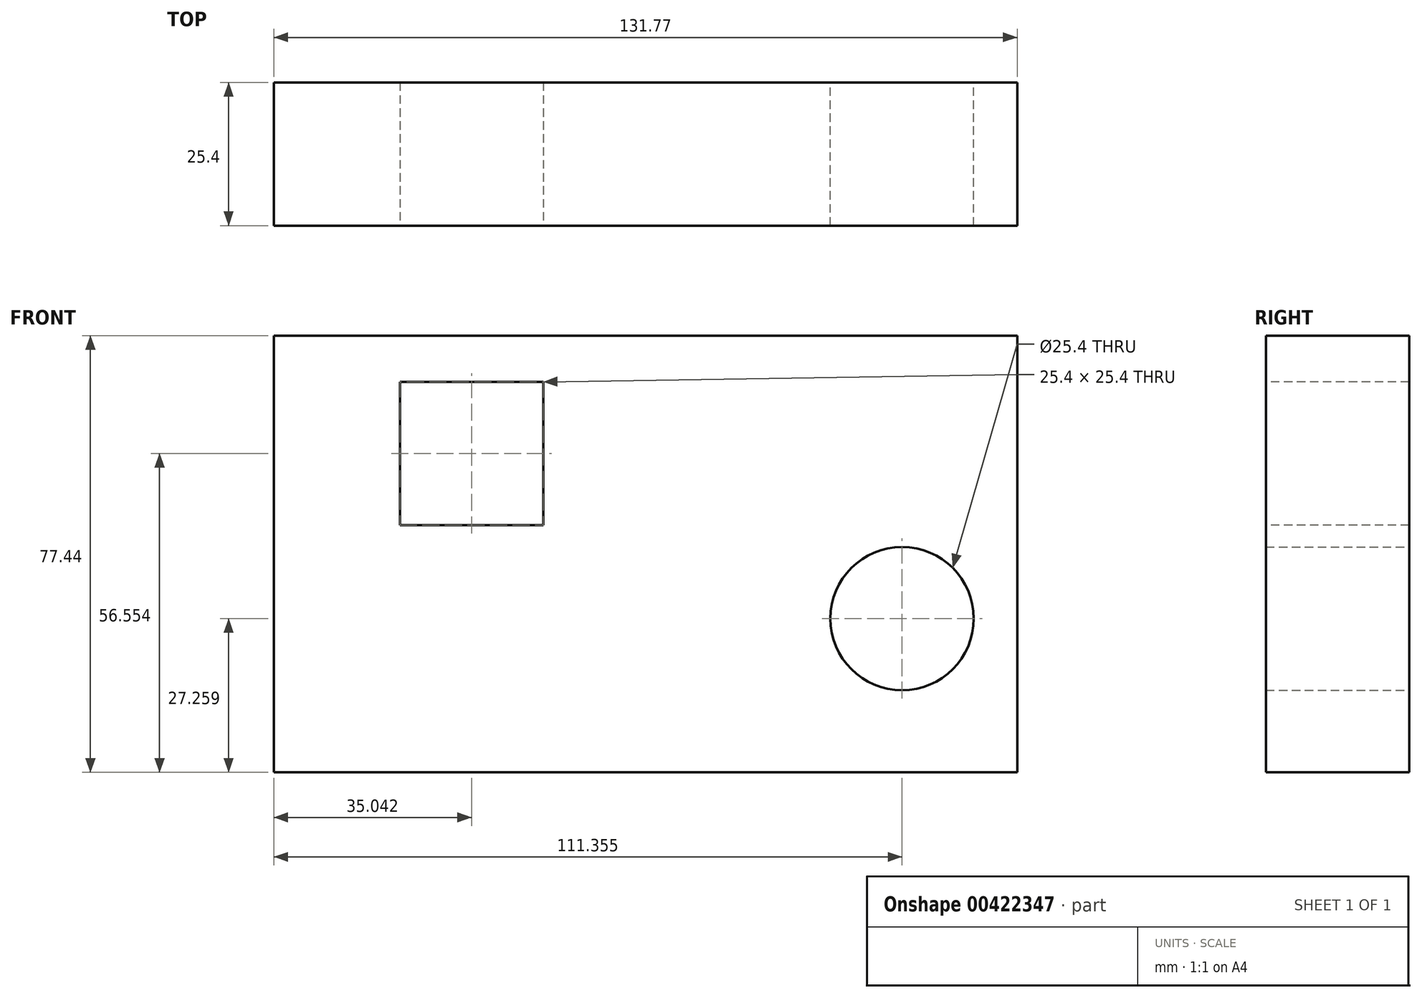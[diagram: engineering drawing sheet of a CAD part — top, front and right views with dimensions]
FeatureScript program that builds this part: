
annotation { "Feature Type Name" : "Feature", "Feature Type Description" : "" }
export const myFeature = defineFeature(function(context is Context, id is Id, definition is map)
    precondition{}
    {
        {
            var Q0;
            Q0=qCreatedBy(makeId("Front.planeOp"),FACE);
            var sketch = newSketch(context, id + "F0", { "sketchPlane" : qUnion([Q0])});
            skLineSegment(sketch, "E0.bottom", {"start": v(-55.32, 38.92) * mm, "end": v(76.45, 38.92) * mm});
            skLineSegment(sketch, "E0.top", {"start": v(-55.32, -38.52) * mm, "end": v(76.45, -38.52) * mm});
            skLineSegment(sketch, "E0.left", {"start": v(-55.32, 38.92) * mm, "end": v(-55.32, -38.52) * mm});
            skLineSegment(sketch, "E0.right", {"start": v(76.45, 38.92) * mm, "end": v(76.45, -38.52) * mm});
            skSolve(sketch);
        }
        {
            var Q0;
            Q0 = qSketchRegion(id + "F0", true);
            extrude(context, id + "F1", {"entities" : qUnion([Q0]), "depth" : 25.4 * mm});
        }
        {
            var Q0;
            Q0=qCreatedBy(makeId("Front.planeOp"),FACE);
            var sketch = newSketch(context, id + "F2", { "sketchPlane" : qUnion([Q0])});
            skCircle(sketch, "E1", {"center": v(56.04, -11.26) * mm, "radius": 12.7 * mm});
            skSolve(sketch);
        }
        {
            var Q0;
            Q0 = qSketchRegion(id + "F2", true);
            extrude(context, id + "F3", {"entities" : qUnion([Q0]), "operationType" : NewBodyOperationType.REMOVE, "depth" : 25.4 * mm});
        }
        {
            var Q0;
            Q0=makeQuery(id+"F1.opExtrude","CAP_FACE",FACE,{"disambiguationData":[OSD([sQuery(id+"F0.wireOp",EDGE,"E0.bottom"),sQuery(id+"F0.wireOp",EDGE,"E0.top"),sQuery(id+"F0.wireOp",EDGE,"E0.left"),sQuery(id+"F0.wireOp",EDGE,"E0.right")])],"isStart":false});
            var sketch = newSketch(context, id + "F4", { "sketchPlane" : qUnion([Q0])});
            skLineSegment(sketch, "E2.bottom", {"start": v(-32.98, 30.73) * mm, "end": v(-7.58, 30.73) * mm});
            skLineSegment(sketch, "E2.top", {"start": v(-32.98, 5.33) * mm, "end": v(-7.58, 5.33) * mm});
            skLineSegment(sketch, "E2.left", {"start": v(-32.98, 30.73) * mm, "end": v(-32.98, 5.33) * mm});
            skLineSegment(sketch, "E2.right", {"start": v(-7.58, 30.73) * mm, "end": v(-7.58, 5.33) * mm});
            skSolve(sketch);
        }
        {
            var Q0;
            Q0 = qSketchRegion(id + "F4", true);
            extrude(context, id + "F5", {"entities" : qUnion([Q0]), "operationType" : NewBodyOperationType.REMOVE, "oppositeDirection" : true, "depth" : 25.4 * mm});
        }
    });
